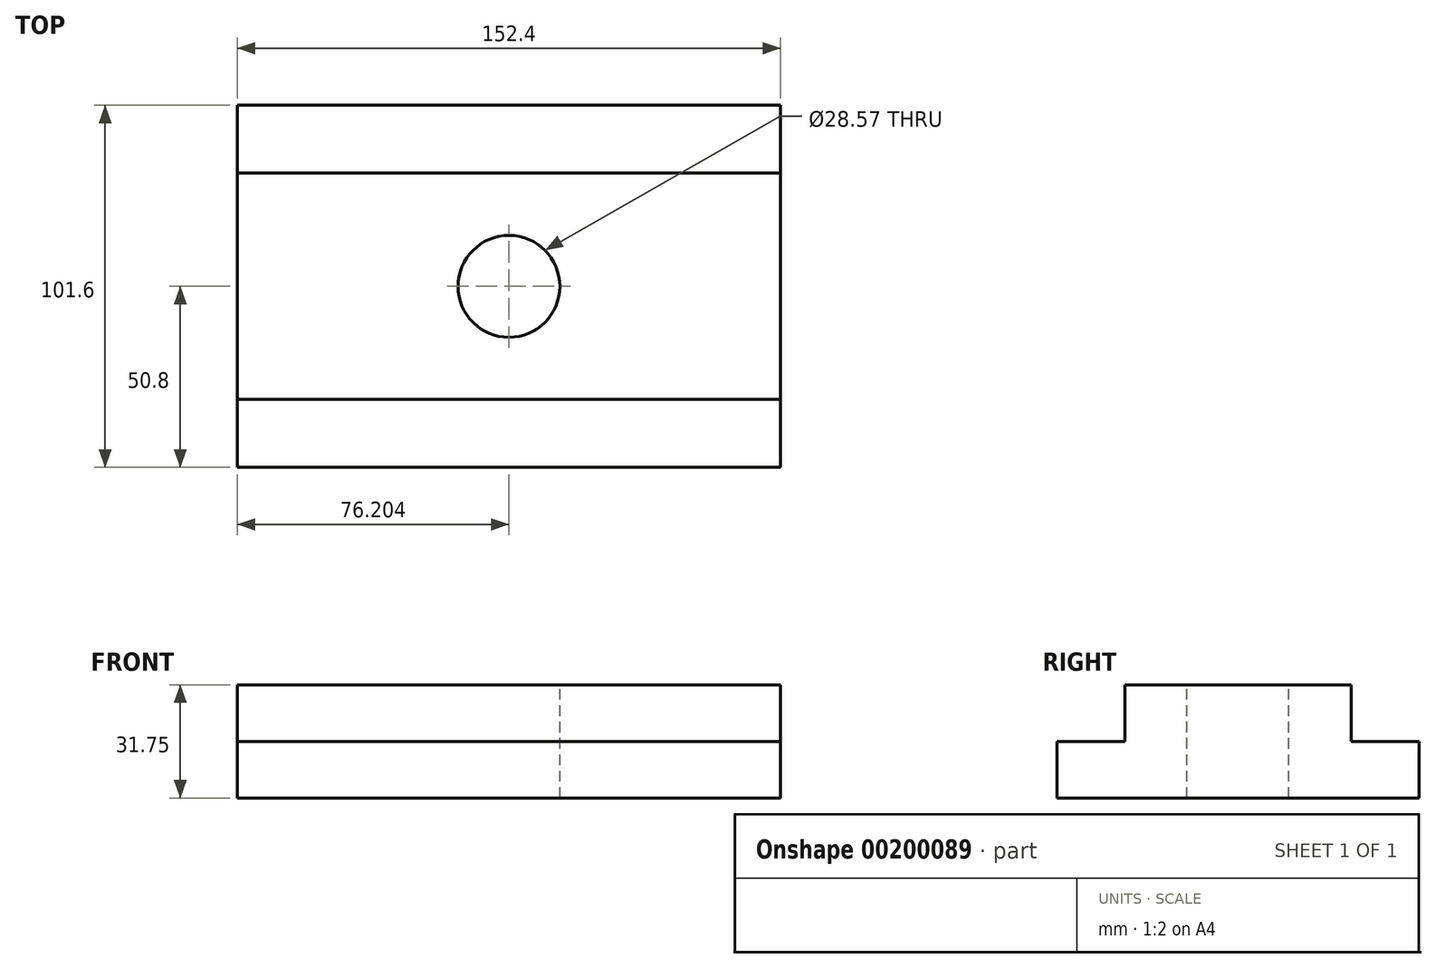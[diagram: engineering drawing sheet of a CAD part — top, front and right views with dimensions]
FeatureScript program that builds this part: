
annotation { "Feature Type Name" : "Feature", "Feature Type Description" : "" }
export const myFeature = defineFeature(function(context is Context, id is Id, definition is map)
    precondition{}
    {
        {
            var Q0;
            Q0=qCreatedBy(makeId("Top.planeOp"),FACE);
            var sketch = newSketch(context, id + "F0", { "sketchPlane" : qUnion([Q0])});
            skLineSegment(sketch, "E0", {"start": v(-70.64, 0) * mm, "end": v(81.76, 0) * mm});
            skLineSegment(sketch, "E1", {"start": v(81.76, 0) * mm, "end": v(81.76, 101.6) * mm});
            skLineSegment(sketch, "E2", {"start": v(81.76, 101.6) * mm, "end": v(-70.64, 101.6) * mm});
            skLineSegment(sketch, "E3", {"start": v(-70.64, 0) * mm, "end": v(-70.64, 101.6) * mm});
            skSolve(sketch);
        }
        {
            var Q0;
            Q0=makeQuery(id+"F0.imprint","IMPRINT",FACE,{"disambiguationData":[TD([[makeQuery(id+"F0.imprint","IMPRINT",EDGE,{"derivedFrom":sQuery(id+"F0.wireOp",EDGE,"E0")}),1.0]])]});
            extrude(context, id + "F1", {"entities" : qUnion([Q0]), "depth" : 15.88 * mm});
        }
        {
            var Q0;
            Q0=makeQuery(id+"F1.opExtrude","CAP_FACE",FACE,{"disambiguationData":[OSD([sQuery(id+"F0.wireOp",EDGE,"E0"),sQuery(id+"F0.wireOp",EDGE,"E1"),sQuery(id+"F0.wireOp",EDGE,"E2"),sQuery(id+"F0.wireOp",EDGE,"E3")])],"isStart":false});
            var sketch = newSketch(context, id + "F2", { "sketchPlane" : qUnion([Q0])});
            skPoint(sketch, "E4", {"position": v(-70.64, 50.8) * mm});
            skPoint(sketch, "E5", {"position": v(81.76, 50.8) * mm});
            skPoint(sketch, "E6", {"position": v(5.56, 50.8) * mm});
            skPoint(sketch, "E7", {"position": v(-70.64, 19.05) * mm});
            skPoint(sketch, "E8", {"position": v(81.76, 19.05) * mm});
            skPoint(sketch, "E9", {"position": v(81.76, 82.55) * mm});
            skPoint(sketch, "E10", {"position": v(-70.64, 82.55) * mm});
            skLineSegment(sketch, "E11", {"start": v(-70.64, 82.55) * mm, "end": v(81.76, 82.55) * mm});
            skLineSegment(sketch, "E12", {"start": v(-70.64, 19.05) * mm, "end": v(81.76, 19.05) * mm});
            skSolve(sketch);
        }
        {
            var Q0;
            {var subQ0=sQuery(id+"F2.wireOp",EDGE,"E11");Q0=makeQuery(id+"F2.imprint","IMPRINT",FACE,{"disambiguationData":[TD([[makeQuery(id+"F2.imprint","IMPRINT",EDGE,{"derivedFrom":subQ0}),-1.0]])]});}
            extrude(context, id + "F3", {"entities" : qUnion([Q0]), "operationType" : NewBodyOperationType.ADD, "depth" : 15.88 * mm});
        }
        {
            var Q0;
            Q0=makeQuery(id+"F3.opExtrude","CAP_FACE",FACE,{"disambiguationData":[OSD([sQuery(id+"F0.wireOp",EDGE,"E1"),sQuery(id+"F0.wireOp",EDGE,"E3"),sQuery(id+"F2.wireOp",EDGE,"E11"),sQuery(id+"F2.wireOp",EDGE,"E12")])],"isStart":false});
            var sketch = newSketch(context, id + "F4", { "sketchPlane" : qUnion([Q0])});
            skPoint(sketch, "E13", {"position": v(-70.64, 50.8) * mm});
            skPoint(sketch, "E14", {"position": v(81.76, 50.8) * mm});
            skPoint(sketch, "E15.center.orphan", {"position": v(0, 50.8) * mm});
            skPoint(sketch, "E16", {"position": v(5.56, 50.8) * mm});
            skCircle(sketch, "E17", {"center": v(5.56, 50.8) * mm, "radius": 14.29 * mm});
            skSolve(sketch);
        }
        {
            var Q0;
            Q0=sQuery(id+"F4.wireOp",VERTEX,"E16");
            var Q1;
            Q1=makeQuery(id+"F1.opExtrude","SWEPT_BODY",BODY,{"disambiguationData":[OSD([sQuery(id+"F0.wireOp",EDGE,"E0"),sQuery(id+"F0.wireOp",EDGE,"E1"),sQuery(id+"F0.wireOp",EDGE,"E2"),sQuery(id+"F0.wireOp",EDGE,"E3")])]});
            hole(context, id + "F5", {"style" : HoleStyle.SIMPLE, "endStyle" : HoleEndStyle.THROUGH, "holeDiameter" : 28.57 * mm, "locations" : qUnion([Q0]), "scope" : qUnion([Q1]), "isTappedThrough" : true});
        }
    });
